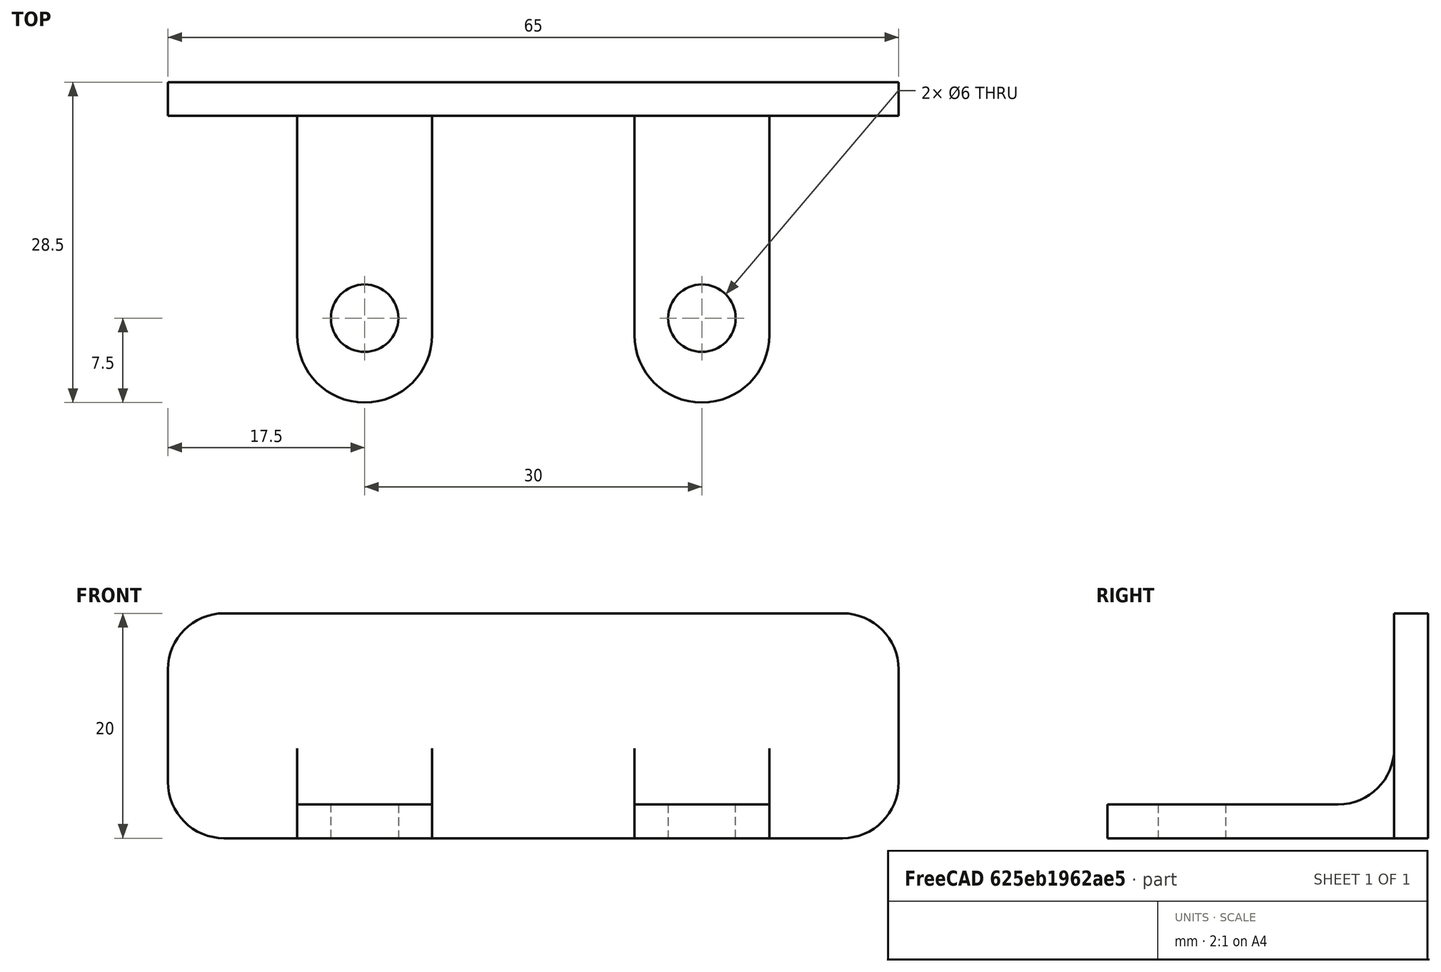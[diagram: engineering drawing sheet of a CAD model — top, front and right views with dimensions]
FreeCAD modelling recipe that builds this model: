
FCSTD DOCUMENT  (FreeCAD 0.19R24291 (Git))
Label: держатель для иголок2
License: All rights reserved
LicenseURL: http://en.wikipedia.org/wiki/All_rights_reserved
objects: Sketcher::SketchObject×3, PartDesign::Pad×3, PartDesign::Body×1, PartDesign::Mirrored×1
note: 11 computed .brp shape members not serialized (recipe doc carries the construction recipe); baked Part::Feature solids carry a one-line shape summary decoded from their .brp

FEATURE [Sketcher::SketchObject] Sketch
  FullyConstrained = true
  MapMode = 5
  Support = -> [XY_Plane]
  sketch-geometry (7):
    g0: Circle CenterX=15 CenterY=0 CenterZ=0 NormalX=0 NormalY=0 NormalZ=1 AngleXU=0 Radius=3
    g1: ArcOfCircle CenterX=15 CenterY=-1.5 CenterZ=0 NormalX=0 NormalY=0 NormalZ=1 AngleXU=0 Radius=6 StartAngle=3.14159 EndAngle=6.28319
    g2: LineSegment StartX=15 StartY=0 StartZ=0 EndX=15 EndY=-1.5 EndZ=0
    g3: LineSegment StartX=15 StartY=-1.5 StartZ=0 EndX=15 EndY=-3 EndZ=0
    g4: LineSegment StartX=21 StartY=-1.5 StartZ=0 EndX=21 EndY=18 EndZ=0
    g5: LineSegment StartX=9 StartY=-1.50001 StartZ=0 EndX=9 EndY=18 EndZ=0
    g6: LineSegment StartX=21 StartY=18 StartZ=0 EndX=9 EndY=18 EndZ=0
  constraints (21):
    c: PointOnObject(g0,g-1)
    c: Coincident(g2,g0)
    c: Coincident(g2,g1)
    c: Vertical(g2)
    c: Coincident(g3,g1)
    c: PointOnObject(g3,g0)
    c: Vertical(g3)
    c: Equal(g3,g2)
    c: Distance(g0,g-1) = 15
    c: Diameter(g0) = 6
    c: Diameter(g1) = 12
    c: Coincident(g4,g1)
    c: Vertical(g4)
    c: Coincident(g5,g1)
    c: Vertical(g5)
    c: Tangent(g1,g4)
    c: Tangent(g1,g5)
    c: Coincident(g6,g4)
    c: Coincident(g6,g5)
    c: Horizontal(g6)
    c: DistanceY(g0,g4) = 18
FEATURE [PartDesign::Pad] Pad
  Direction = (1,1,1)
  Length = 3
  Length2 = 100
  Profile = -> Sketch
  Type = 0
FEATURE [Sketcher::SketchObject] Sketch001
  FullyConstrained = true
  MapMode = 5
  Placement = pos=(0,18,0) rot=(0,0.707107,0.707107;3.14159rad)
  Support = -> [Pad]
  sketch-geometry (7):
    g0: LineSegment StartX=0 StartY=0 StartZ=0 EndX=-27.5 EndY=0 EndZ=0
    g1: LineSegment StartX=-32.5 StartY=5 StartZ=0 EndX=-32.5 EndY=15 EndZ=0
    g2: LineSegment StartX=-27.5 StartY=20 StartZ=0 EndX=0 EndY=20 EndZ=0
    g3: LineSegment StartX=0 StartY=20 StartZ=0 EndX=0 EndY=0 EndZ=0
    g4: ArcOfCircle CenterX=-27.5 CenterY=15 CenterZ=0 NormalX=0 NormalY=0 NormalZ=1 AngleXU=0 Radius=5 StartAngle=1.5708 EndAngle=3.14159
    g5: ArcOfCircle CenterX=-27.5 CenterY=5 CenterZ=0 NormalX=0 NormalY=0 NormalZ=1 AngleXU=0 Radius=5 StartAngle=3.14159 EndAngle=4.71239
    g6: LineSegment StartX=-32.5 StartY=5 StartZ=0 EndX=0 EndY=5 EndZ=0
  constraints (18):
    c: Coincident(g2,g3)
    c: Coincident(g3,g0)
    c: Horizontal(g0)
    c: Horizontal(g2)
    c: Vertical(g1)
    c: Vertical(g3)
    c: Coincident(g0,g-1)
    c: Tangent(g2,g4) = 1.5708
    c: Tangent(g1,g4) = 1.5708
    c: Tangent(g0,g5) = 1.5708
    c: Tangent(g1,g5) = 1.5708
    c: DistanceY(g0,g2) = 20
    c: Equal(g5,g4)
    c: Diameter(g5) = 10
    c: Coincident(g6,g1)
    c: PointOnObject(g6,g3)
    c: Horizontal(g6)
    c: Distance(g6) = 32.5
FEATURE [PartDesign::Pad] Pad001
  BaseFeature = -> Pad
  Direction = (1,1,1)
  Length = 3
  Length2 = 100
  Profile = -> Sketch001
  Type = 0
FEATURE [Sketcher::SketchObject] Sketch002
  ExternalGeometry = -> [Pad001]
  FullyConstrained = true
  MapMode = 5
  Placement = pos=(21,0,0) rot=(0.57735,0.57735,0.57735;2.0944rad)
  Support = -> [Pad001]
  sketch-geometry (3):
    g0: ArcOfCircle CenterX=13 CenterY=8 CenterZ=0 NormalX=0 NormalY=0 NormalZ=1 AngleXU=0 Radius=5 StartAngle=4.71239 EndAngle=6.28319
    g1: LineSegment StartX=18 StartY=3 StartZ=0 EndX=18 EndY=8 EndZ=0
    g2: LineSegment StartX=13 StartY=3 StartZ=0 EndX=18 EndY=3 EndZ=0
  constraints (9):
    c: PointOnObject(g0,g-3)
    c: Coincident(g1,g-3)
    c: Vertical(g1)
    c: Coincident(g0,g1)
    c: Coincident(g2,g0)
    c: Coincident(g2,g1)
    c: Tangent(g0,g1)
    c: Tangent(g0,g2)
    c: Diameter(g0) = 10
FEATURE [PartDesign::Body] Body
  Group = -> [Sketch,Pad,Sketch001,Pad001,Mirrored,Sketch002,Pad002]
  Origin = -> Origin
  Tip = -> Pad002
FEATURE [PartDesign::Mirrored] Mirrored
  BaseFeature = -> Pad001
  MirrorPlane = -> Sketch [V_Axis]
  Originals = -> [Pad001,Pad,Pad002]
FEATURE [PartDesign::Pad] Pad002
  BaseFeature = -> Mirrored
  Direction = (1,1,1)
  Length = 10
  Length2 = 100
  Profile = -> Sketch002
  Type = 3
  UpToFace = -> Mirrored [Face14]
